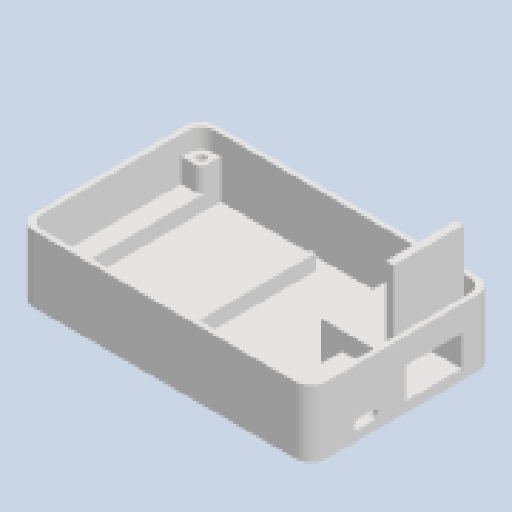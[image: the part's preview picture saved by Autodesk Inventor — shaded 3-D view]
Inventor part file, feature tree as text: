
AUTODESK INVENTOR PART (.ipt)
format: ipt  version: 2025.2 (Build 292293000, 293)  size: 406,016 bytes
history: native  units: mm
features: extrude x15, sketch x13, fillet x1, plane x1, hole x1
ambient origin geometry x8: Origin, YZ Plane, XZ Plane, XY Plane, X Axis, Y Axis, Z Axis, Center Point
bodies: Solid1 (feature_tree)
feature tree (31):
  extrude  "Extrusion1"  Depth=67.5mm
  fillet  "Fillet1"  Radius=3.0mm
  extrude  "Extrusion2"  Depth=2.0mm
  extrude  "Extrusion3"  Depth=6.25mm
  extrude  "Extrusion4"  Depth=26.0mm TaperAngle=0.0deg
  plane  "Work Plane1"
  extrude  "Extrusion5"  Depth=27.5mm
  extrude  "Extrusion6"  Depth=3.0mm TaperAngle=0.0deg
  sketch  "Sketch7"  dims[d16=5.0mm d17=5.0mm]
  extrude  "Extrusion7"  Depth=5.0mm
  extrude  "Extrusion8"  [1 undecoded]
  extrude  "Extrusion9"  Depth=40.0mm
  sketch  "Sketch8"  dims[d18=15.25mm d19=0.0mm d20=-7.0mm]
  extrude  "Extrusion10"  Depth=30.0mm
  extrude  "Extrusion11"  Depth=14.0mm
  extrude  "Extrusion12"  Depth=7.0mm
  extrude  "Extrusion13"  Depth=12.0mm
  extrude  "Extrusion14"  Depth=4.0mm
  extrude  "Extrusion15"  Depth=13.0mm TaperAngle=0.0deg
  hole  "Hole2"  [1 undecoded]
  sketch  "Sketch1"  dims[d0=110.52mm d1=67.5mm d2=3.0mm d3=0.0mm]
  sketch  "Sketch2"  dims[d4=5.25mm d5=2.0mm]
  sketch  "Sketch3"  dims[d6=2.0mm d7=6.25mm]
  sketch  "Sketch4"  dims[d8=6.25mm d9=26.0mm d10=0.0mm]
  sketch  "Sketch5"  dims[d11=7.75mm d12=27.5mm]
  sketch  "Sketch6"  dims[d13=24.408mm d14=3.0mm d15=0.0mm]
  sketch  "Sketch9"  dims[d21=2.0mm d22=40.0mm]
  sketch  "Sketch10"  dims[d27=6.0mm d28=0.0mm d29=30.0mm]
  sketch  "Sketch11"  dims[d30=14.0mm d31=0.0mm d32=14.0mm]
  sketch  "Sketch12"  dims[d33=9.0mm d34=7.0mm]
  sketch  "Sketch14"  dims[d35=22.0mm d36=12.0mm d37=4.0mm d38=13.0mm d39=0.0mm d40=20.0mm d41=0.0mm d42=20.0mm d43=0.0mm d44=18.0mm d45=27.5mm d46=8.0mm d48=35.0mm d49=18.5mm d52=7.0mm d53=7.0mm d54=5.5mm d55=10.0mm d56=17.0mm d57=10.0mm d58=0.0mm d59=2.0mm d60=4.0mm d61=3.5mm d62=9.5mm d63=7.0mm d64=0.75mm d65=10.0mm d66=0.0mm d67=12.5mm d68=6.5mm d69=2.0mm d70=2.0mm d71=2.0mm d72=0.0mm d73=2.0mm d74=0.0mm d75=1.0mm d76=9.0mm d77=8.0mm d78=11.0mm d79=6.0mm d80=1.5mm d81=1.0mm d82=2.0mm d83=1.5mm d84=0.0mm d85=0.0mm d86=0.0mm d94=3.4mm d95=6.0mm d96=7.0mm d97=4.0mm d98=90.0deg d99=8.0mm d100=20.594885mm d102=11.75mm]
note: 2 required parameter values undecoded (feature->parameter linkage not recoverable at this tier; creation-order binding heuristic only, values carry confidence <= 0.55)
